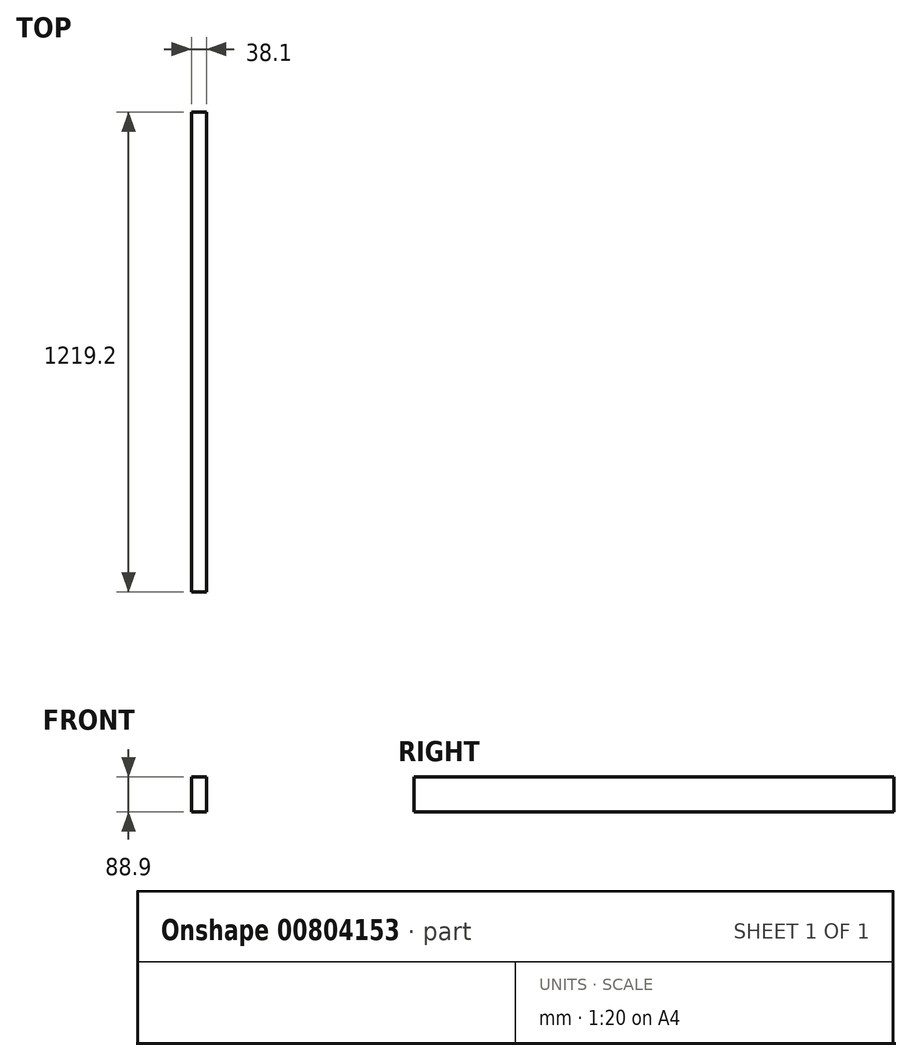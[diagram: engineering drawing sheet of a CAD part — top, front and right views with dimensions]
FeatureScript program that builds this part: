
annotation { "Feature Type Name" : "Feature", "Feature Type Description" : "" }
export const myFeature = defineFeature(function(context is Context, id is Id, definition is map)
    precondition{}
    {
        {
            var Q0;
            Q0=qCreatedBy(makeId("Front.planeOp"),FACE);
            var sketch = newSketch(context, id + "F0", { "sketchPlane" : qUnion([Q0])});
            skLineSegment(sketch, "E0.bottom", {"start": v(19.05, -44.45) * mm, "end": v(-19.05, -44.45) * mm});
            skLineSegment(sketch, "E0.top", {"start": v(19.05, 44.45) * mm, "end": v(-19.05, 44.45) * mm});
            skLineSegment(sketch, "E0.left", {"start": v(19.05, -44.45) * mm, "end": v(19.05, 44.45) * mm});
            skLineSegment(sketch, "E0.right", {"start": v(-19.05, -44.45) * mm, "end": v(-19.05, 44.45) * mm});
            skPoint(sketch, "E0.middle", {"position": v(0, 0) * mm});
            skSolve(sketch);
        }
        {
            var Q0;
            Q0 = qSketchRegion(id + "F0", true);
            extrude(context, id + "F1", {"entities" : qUnion([Q0]), "endBound" : BoundingType.SYMMETRIC, "depth" : 1219.2 * mm, "offsetDistance" : 25.4 * mm});
        }
    });
